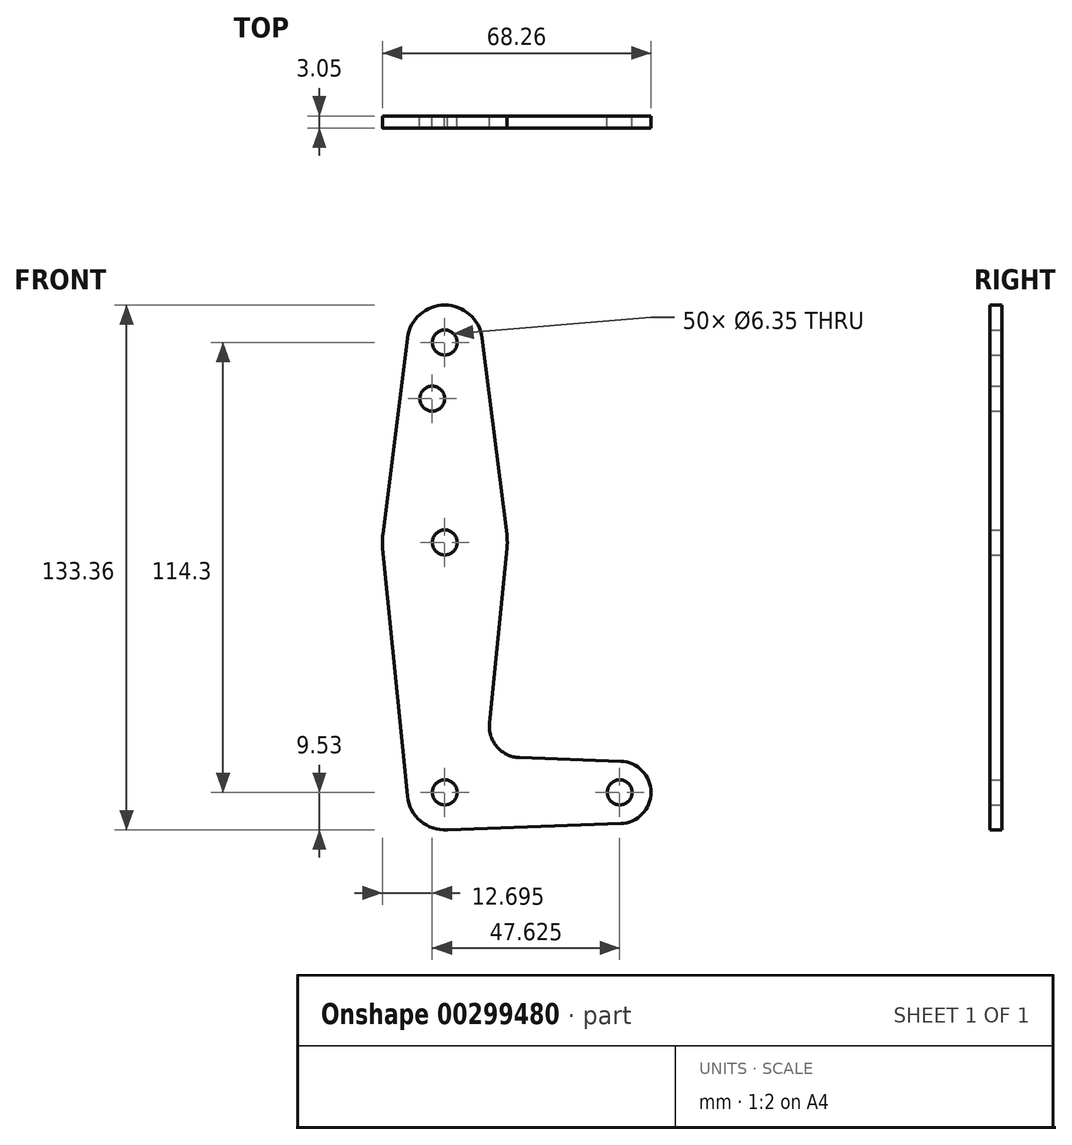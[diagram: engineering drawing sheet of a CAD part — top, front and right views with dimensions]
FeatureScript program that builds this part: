
annotation { "Feature Type Name" : "Feature", "Feature Type Description" : "" }
export const myFeature = defineFeature(function(context is Context, id is Id, definition is map)
    precondition{}
    {
        {
            var Q0;
            Q0=qCreatedBy(makeId("Front.planeOp"),FACE);
            var sketch = newSketch(context, id + "F0", { "sketchPlane" : qUnion([Q0])});
            skCircle(sketch, "E0", {"center": v(0, 0) * mm, "radius": 9.53 * mm});
            skCircle(sketch, "E1", {"center": v(0, 63.5) * mm, "radius": 15.88 * mm});
            skCircle(sketch, "E2", {"center": v(0, 114.3) * mm, "radius": 9.53 * mm});
            skCircle(sketch, "E3", {"center": v(44.45, 0) * mm, "radius": 7.94 * mm});
            skLineSegment(sketch, "E4", {"start": v(0, 114.3) * mm, "end": v(0, 63.5) * mm, "construction": true});
            skLineSegment(sketch, "E5", {"start": v(0, 63.5) * mm, "end": v(0, 0) * mm, "construction": true});
            skLineSegment(sketch, "E6", {"start": v(0, 0) * mm, "end": v(44.45, 0) * mm, "construction": true});
            skLineSegment(sketch, "E7", {"start": v(-9.48, -0.95) * mm, "end": v(-15.8, 61.91) * mm});
            skLineSegment(sketch, "E8", {"start": v(-9.45, 115.5) * mm, "end": v(-15.75, 65.48) * mm});
            skLineSegment(sketch, "E9", {"start": v(9.45, 115.5) * mm, "end": v(15.75, 65.48) * mm});
            skLineSegment(sketch, "E10", {"start": v(15.8, 61.91) * mm, "end": v(11.34, 17.59) * mm});
            skLineSegment(sketch, "E11", {"start": v(18.97, 8.85) * mm, "end": v(44.73, 7.93) * mm});
            skLineSegment(sketch, "E12", {"start": v(0, -9.53) * mm, "end": v(44.73, -7.93) * mm});
            skCircle(sketch, "E13", {"center": v(0, 114.3) * mm, "radius": 3.18 * mm});
            skCircle(sketch, "E14", {"center": v(-3.18, 100.03) * mm, "radius": 3.18 * mm});
            skCircle(sketch, "E15", {"center": v(0, 63.5) * mm, "radius": 3.18 * mm});
            skCircle(sketch, "E16", {"center": v(0, 0) * mm, "radius": 3.18 * mm});
            skCircle(sketch, "E17", {"center": v(44.45, 0) * mm, "radius": 3.18 * mm});
            skPoint(sketch, "E18.newPointB", {"position": v(0, 9.53) * mm});
            skArc(sketch, "E18.filletArc", {"start": v(11.34, 17.59) * mm, "mid": v(13.26, 11.57) * mm, "end": v(18.97, 8.85) * mm});
            skSolve(sketch);
        }
        {
            var Q0;
            Q0 = qSketchRegion(id + "F0", true);
            extrude(context, id + "F1", {"entities" : qUnion([Q0]), "depth" : 3.05 * mm});
        }
    });
